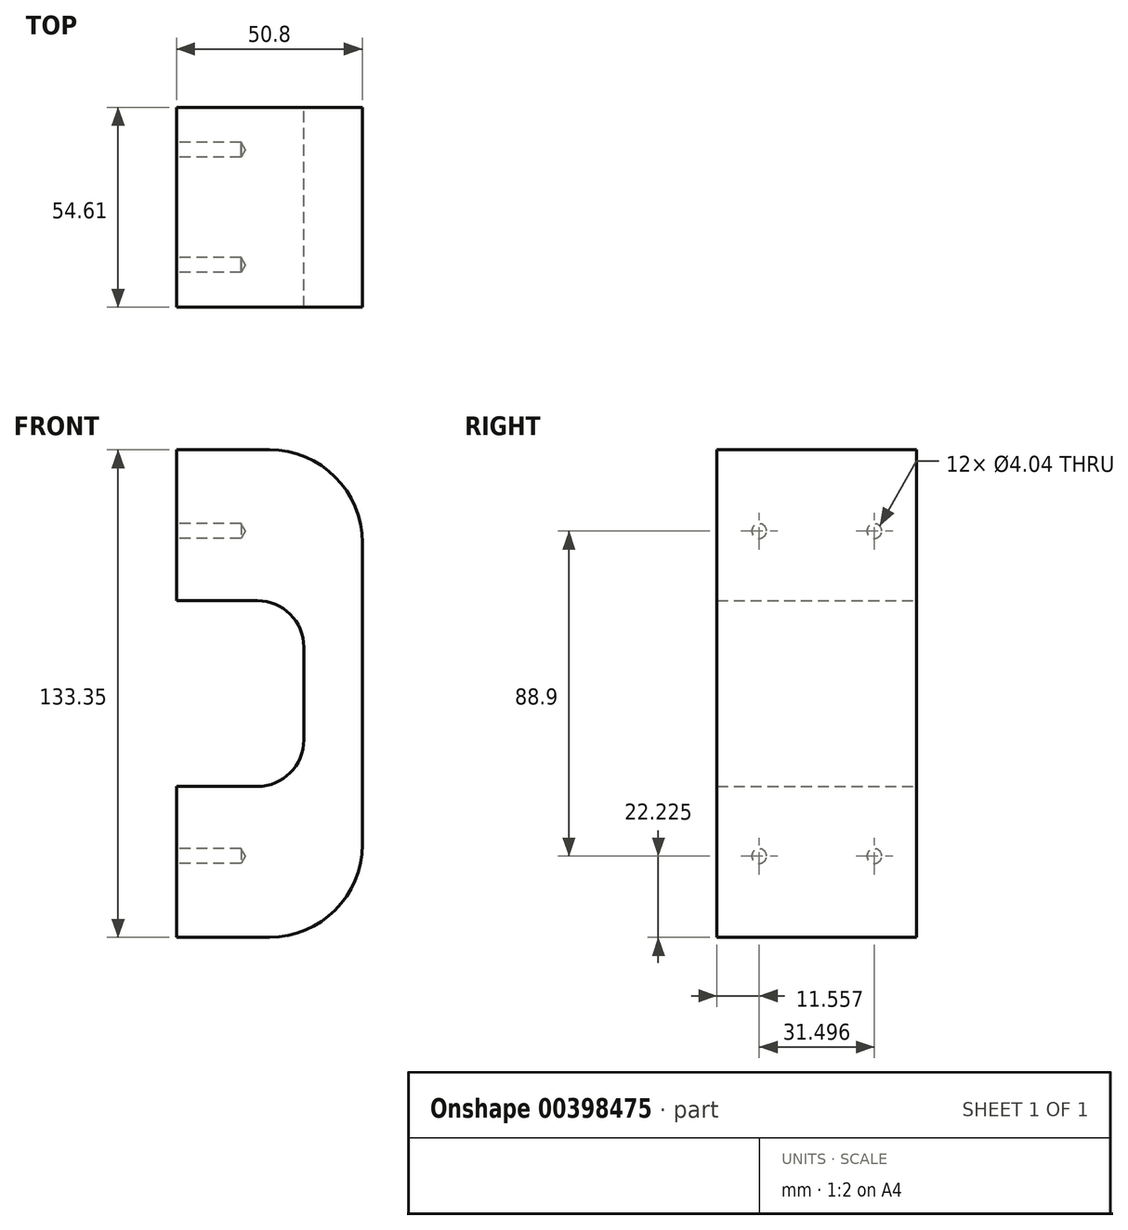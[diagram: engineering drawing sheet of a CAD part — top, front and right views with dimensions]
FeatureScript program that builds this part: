
annotation { "Feature Type Name" : "Feature", "Feature Type Description" : "" }
export const myFeature = defineFeature(function(context is Context, id is Id, definition is map)
    precondition{}
    {
        {
            var Q0;
            Q0=qCreatedBy(makeId("Top.planeOp"),FACE);
            var sketch = newSketch(context, id + "F0", { "sketchPlane" : qUnion([Q0])});
            skLineSegment(sketch, "E0.bottom", {"start": v(0, 0) * mm, "end": v(50.8, 0) * mm});
            skLineSegment(sketch, "E0.top", {"start": v(0, 54.61) * mm, "end": v(50.8, 54.61) * mm});
            skLineSegment(sketch, "E0.left", {"start": v(0, 0) * mm, "end": v(0, 54.61) * mm});
            skLineSegment(sketch, "E0.right", {"start": v(50.8, 0) * mm, "end": v(50.8, 54.61) * mm});
            skSolve(sketch);
        }
        {
            var Q0;
            Q0 = qSketchRegion(id + "F0", true);
            extrude(context, id + "F1", {"entities" : qUnion([Q0]), "depth" : 133.35 * mm});
        }
        {
            var Q0;
            Q0=makeQuery(id+"F1.opExtrude","SWEPT_FACE",FACE,{"disambiguationData":[OSD([sQuery(id+"F0.wireOp",EDGE,"E0.left")])]});
            var sketch = newSketch(context, id + "F2", { "sketchPlane" : qUnion([Q0])});
            skLineSegment(sketch, "E1", {"start": v(-43.05, 133.35) * mm, "end": v(-43.05, 0) * mm, "construction": true});
            skLineSegment(sketch, "E2", {"start": v(-11.56, 0) * mm, "end": v(-43.05, 0) * mm, "construction": true});
            skLineSegment(sketch, "E3", {"start": v(-11.56, 0) * mm, "end": v(-11.56, 133.35) * mm, "construction": true});
            skLineSegment(sketch, "E4", {"start": v(-43.05, 133.35) * mm, "end": v(-11.56, 133.35) * mm, "construction": true});
            skLineSegment(sketch, "E5", {"start": v(0, 22.23) * mm, "end": v(-54.6, 22.23) * mm, "construction": true});
            skLineSegment(sketch, "E6", {"start": v(0, 111.13) * mm, "end": v(-54.6, 111.13) * mm, "construction": true});
            skPoint(sketch, "E7", {"position": v(-11.56, 22.23) * mm});
            skPoint(sketch, "E8", {"position": v(-43.05, 22.23) * mm});
            skPoint(sketch, "E9", {"position": v(-11.56, 111.13) * mm});
            skPoint(sketch, "E10", {"position": v(-43.05, 111.13) * mm});
            skSolve(sketch);
        }
        {
            var Q0;
            Q0=sQuery(id+"F2.wireOp",VERTEX,"E7");
            var Q1;
            Q1=sQuery(id+"F2.wireOp",VERTEX,"E8");
            var Q2;
            Q2=sQuery(id+"F2.wireOp",VERTEX,"E9");
            var Q3;
            Q3=sQuery(id+"F2.wireOp",VERTEX,"E10");
            var Q4;
            Q4=makeQuery(id+"F1.opExtrude","SWEPT_BODY",BODY,{"disambiguationData":[OSD([sQuery(id+"F0.wireOp",EDGE,"E0.bottom"),sQuery(id+"F0.wireOp",EDGE,"E0.top"),sQuery(id+"F0.wireOp",EDGE,"E0.left"),sQuery(id+"F0.wireOp",EDGE,"E0.right")])]});
            hole(context, id + "F3", {"style" : HoleStyle.SIMPLE, "endStyle" : HoleEndStyle.BLIND, "standardTappedOrClearance" : lookupTablePath({ "standard" : "ANSI", "engagement" : "75%", "pitch" : "32 tpi", "size" : "#10", "type" : "Tapped" }), "standardBlindInLast" : lookupTablePath({ "standard" : "ANSI", "engagement" : "75%", "pitch" : "32 tpi", "size" : "#10", "type" : "Tapped" }), "holeDiameter" : 4.04 * mm, "showTappedDepth" : true, "holeDepth" : 17.63 * mm, "isTappedThrough" : true, "tappedDepth" : 15.25 * mm, "tapClearance" : 3, "locations" : qUnion([Q0, Q1, Q2, Q3]), "scope" : qUnion([Q4]), "majorDiameter" : 4.83 * mm});
        }
        {
            var Q0;
            Q0=makeQuery(id+"F1.opExtrude","SWEPT_FACE",FACE,{"disambiguationData":[OSD([sQuery(id+"F0.wireOp",EDGE,"E0.top")])]});
            var sketch = newSketch(context, id + "F4", { "sketchPlane" : qUnion([Q0])});
            skLineSegment(sketch, "E11.bottom", {"start": v(0, 92.08) * mm, "end": v(-22.1, 92.08) * mm});
            skLineSegment(sketch, "E11.top", {"start": v(0, 41.28) * mm, "end": v(-22.1, 41.28) * mm});
            skLineSegment(sketch, "E11.right", {"start": v(-34.8, 79.38) * mm, "end": v(-34.8, 53.98) * mm});
            skPoint(sketch, "E12.visualSharp", {"position": v(-34.8, 92.08) * mm});
            skArc(sketch, "E12.filletArc", {"start": v(-22.1, 92.08) * mm, "mid": v(-31.08, 88.36) * mm, "end": v(-34.8, 79.38) * mm});
            skPoint(sketch, "E13.visualSharp", {"position": v(-34.8, 41.28) * mm});
            skArc(sketch, "E13.filletArc", {"start": v(-34.8, 53.98) * mm, "mid": v(-31.08, 45) * mm, "end": v(-22.1, 41.27) * mm});
            skLineSegment(sketch, "E14", {"start": v(0, 41.28) * mm, "end": v(0, 0) * mm});
            skLineSegment(sketch, "E15", {"start": v(0, 0) * mm, "end": v(-25.4, 0) * mm});
            skLineSegment(sketch, "E16", {"start": v(-50.8, 25.4) * mm, "end": v(-50.8, 107.95) * mm});
            skLineSegment(sketch, "E17", {"start": v(-25.4, 133.35) * mm, "end": v(0, 133.35) * mm});
            skLineSegment(sketch, "E18", {"start": v(0, 133.35) * mm, "end": v(0, 92.08) * mm});
            skPoint(sketch, "E19.visualSharp", {"position": v(-50.8, 0) * mm});
            skArc(sketch, "E19.filletArc", {"start": v(-50.8, 25.4) * mm, "mid": v(-43.36, 7.44) * mm, "end": v(-25.4, 0) * mm});
            skPoint(sketch, "E20.visualSharp", {"position": v(-50.8, 133.35) * mm});
            skArc(sketch, "E20.filletArc", {"start": v(-25.4, 133.35) * mm, "mid": v(-43.36, 125.91) * mm, "end": v(-50.8, 107.95) * mm});
            skSolve(sketch);
        }
        {
            var Q0;
            Q0 = qSketchRegion(id + "F4", true);
            extrude(context, id + "F5", {"entities" : qUnion([Q0]), "operationType" : NewBodyOperationType.INTERSECT, "endBound" : BoundingType.THROUGH_ALL, "oppositeDirection" : true, "depth" : 25.4 * mm});
        }
    });
